# Revit family: Sanitary_Showers_hansgrohe_24181XXX-Pulsify-Blend-Shower-set-105-3j_
name_source: partatom
category: Plumbing Fixtures
revit_build: Autodesk Revit 2018 (Build: 20170223_1515(x64)
units: mm (PartAtom-declared; Revit-internal decimal feet)

## family parameters
Always vertical = No
Cut with Voids When Loaded = No
OmniClass Number = 23.45.00.00
OmniClass Title = Sanitary, Laundry, and Cleaning Equipment
Part Type = Normal
Room Calculation Point = No
Round Connector Dimension = Use Diameter
Shared = No
Work Plane-Based = Yes

## types (1)
- 000 Chrome
    Always visible = Yes
    BIMobject category = Showers
    Default Elevation = 1219.2 mm  [stored 4 ft]
    Design country = Germany
    EAN code = 4059625347997
    Edition number = 1
    IFC Classification = Sanitary Terminal
    Installation instructions = https://www.hansgrohe.com
    Manufacturer country = Germany
    Manufacturer name = hansgrohe
    Material 1 = Hansgrohe - Pulsify - 000 Chrome
    Material 2 = Hansgrohe - Pulsify - Graphite
    Material main = Chrome
    Product Guid = 60eedd1e-5207-4037-869c-3744753c7389
    Product SKU = 24181XXX
    Product data url = https://www.bimobject.com
    Product family = Pulsify Blend
    Product group = Wallbar sets
    Product name = 24181XXX Pulsify Blend Shower set 105 3jet Relaxation EcoSmart with shower bar 105 cm
    Product url = https://www.hansgrohe.com
    QR code = https://www.bimobject.com
    Technical description = https://www.hansgrohe.com

note: [stored X ft] marks values corroborated as IEEE doubles in the binary element streams (Revit-internal decimal feet)

## geometry (parser evidence)
native form markers: Sweep x3
no freeform markers — native parametric forms only
